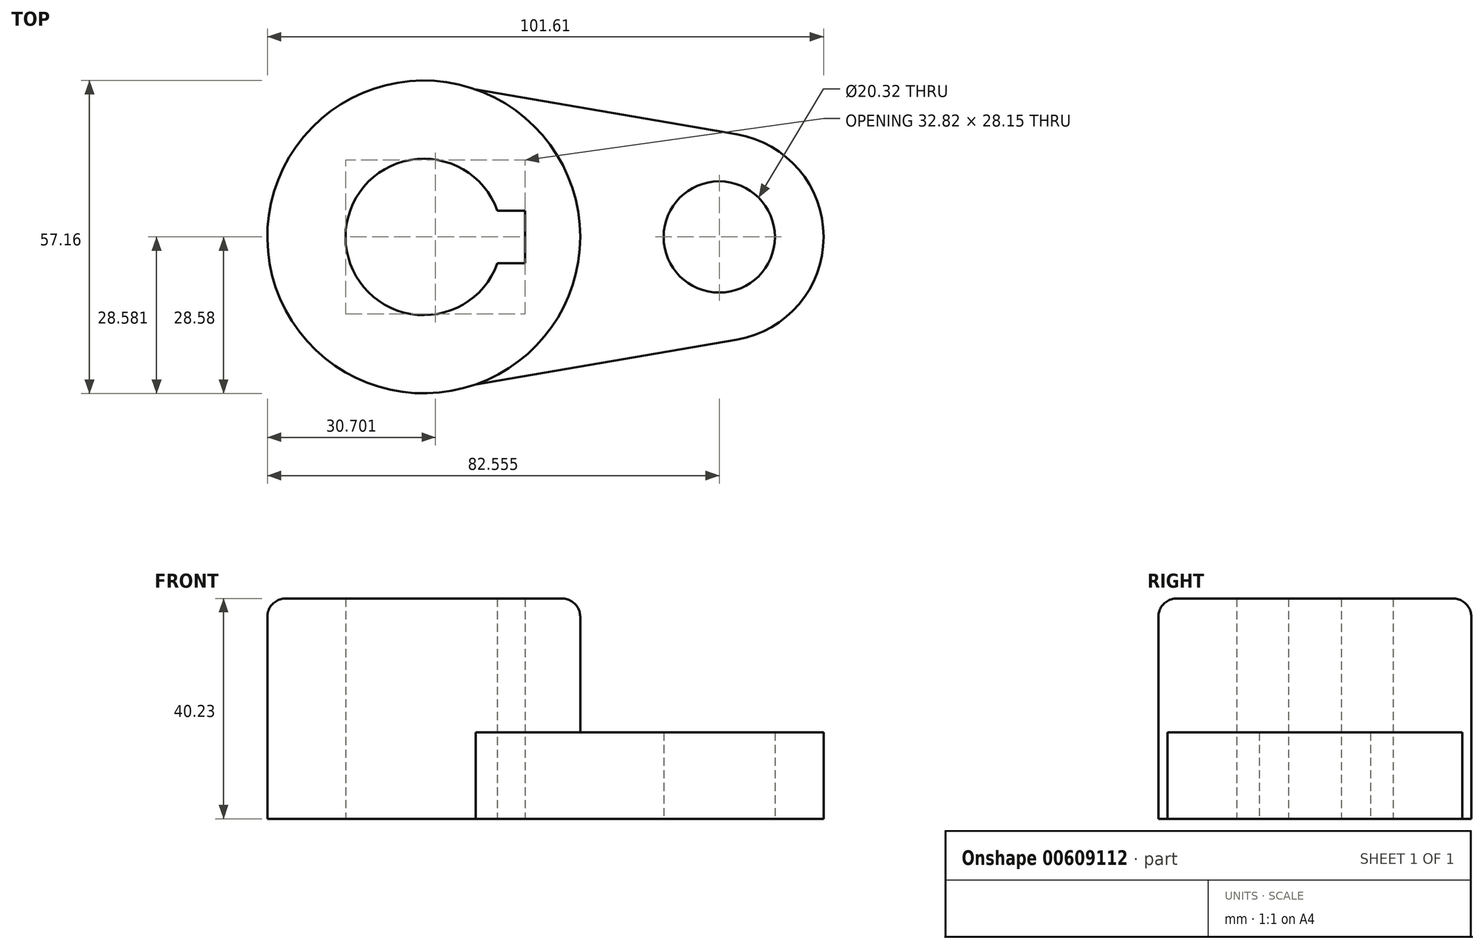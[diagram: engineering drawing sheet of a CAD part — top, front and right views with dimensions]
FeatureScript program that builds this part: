
annotation { "Feature Type Name" : "Feature", "Feature Type Description" : "" }
export const myFeature = defineFeature(function(context is Context, id is Id, definition is map)
    precondition{}
    {
        {
            var Q0;
            Q0=qCreatedBy(makeId("Top.planeOp"),FACE);
            var sketch = newSketch(context, id + "F0", { "sketchPlane" : qUnion([Q0])});
            skArc(sketch, "E0", {"start": v(9.51, -26.95) * mm, "mid": v(28.58, 0) * mm, "end": v(9.51, 26.95) * mm});
            skLineSegment(sketch, "E1", {"start": v(0, 0) * mm, "end": v(53.98, 0) * mm});
            skCircle(sketch, "E2", {"center": v(53.98, 0) * mm, "radius": 10.16 * mm});
            skArc(sketch, "E3", {"start": v(57.2, -18.78) * mm, "mid": v(73.03, 0) * mm, "end": v(57.2, 18.78) * mm});
            skLineSegment(sketch, "E4", {"start": v(9.51, 26.95) * mm, "end": v(57.2, 18.78) * mm});
            skLineSegment(sketch, "E5", {"start": v(9.51, -26.95) * mm, "end": v(57.2, -18.78) * mm});
            skPoint(sketch, "E6.orphan", {"position": v(0, -28.58) * mm});
            skPoint(sketch, "E7.orphan", {"position": v(0, 28.58) * mm});
            skSolve(sketch);
        }
        {
            var Q0;
            Q0=makeQuery(id+"F0.imprint","IMPRINT",FACE,{"disambiguationData":[TD([[makeQuery(id+"F0.imprint","IMPRINT",EDGE,{"derivedFrom":sQuery(id+"F0.wireOp",EDGE,"E2")}),-1.0]])]});
            extrude(context, id + "F1", {"entities" : qUnion([Q0]), "depth" : 15.77 * mm, "offsetDistance" : 25.4 * mm});
        }
        {
            var Q0;
            Q0=qCreatedBy(makeId("Top.planeOp"),FACE);
            var sketch = newSketch(context, id + "F2", { "sketchPlane" : qUnion([Q0])});
            skCircle(sketch, "E8", {"center": v(0, 0) * mm, "radius": 28.58 * mm});
            skArc(sketch, "E9", {"start": v(13.45, 4.82) * mm, "mid": v(-14.29, 0) * mm, "end": v(13.45, -4.83) * mm});
            skLineSegment(sketch, "E10.right", {"start": v(18.53, 4.82) * mm, "end": v(18.53, -4.83) * mm});
            skLineSegment(sketch, "E11.trimOffspring", {"start": v(13.45, 4.82) * mm, "end": v(18.53, 4.82) * mm});
            skLineSegment(sketch, "E12.trimOffspring", {"start": v(13.45, -4.83) * mm, "end": v(18.53, -4.83) * mm});
            skLineSegment(sketch, "E13", {"start": v(0, 0) * mm, "end": v(18.53, 0) * mm});
            skSolve(sketch);
        }
        {
            var Q0;
            Q0=makeQuery(id+"F2.imprint","IMPRINT",FACE,{"disambiguationData":[TD([[makeQuery(id+"F2.imprint","IMPRINT",EDGE,{"derivedFrom":sQuery(id+"F2.wireOp",EDGE,"E8")}),1.0]])]});
            extrude(context, id + "F3", {"entities" : qUnion([Q0]), "operationType" : NewBodyOperationType.ADD, "depth" : 40.23 * mm, "offsetDistance" : 25.4 * mm});
        }
        {
            var Q0;
            Q0=makeQuery(id+"F3.opExtrude","CAP_EDGE",EDGE,{"disambiguationData":[OSD([sQuery(id+"F2.wireOp",EDGE,"E8")])],"isStart":false});
            fillet(context, id + "F4", {"entities" : qUnion([Q0]), "radius" : 3.3 * mm, "tangentPropagation" : true, "allowEdgeOverflow" : false});
        }
    });
